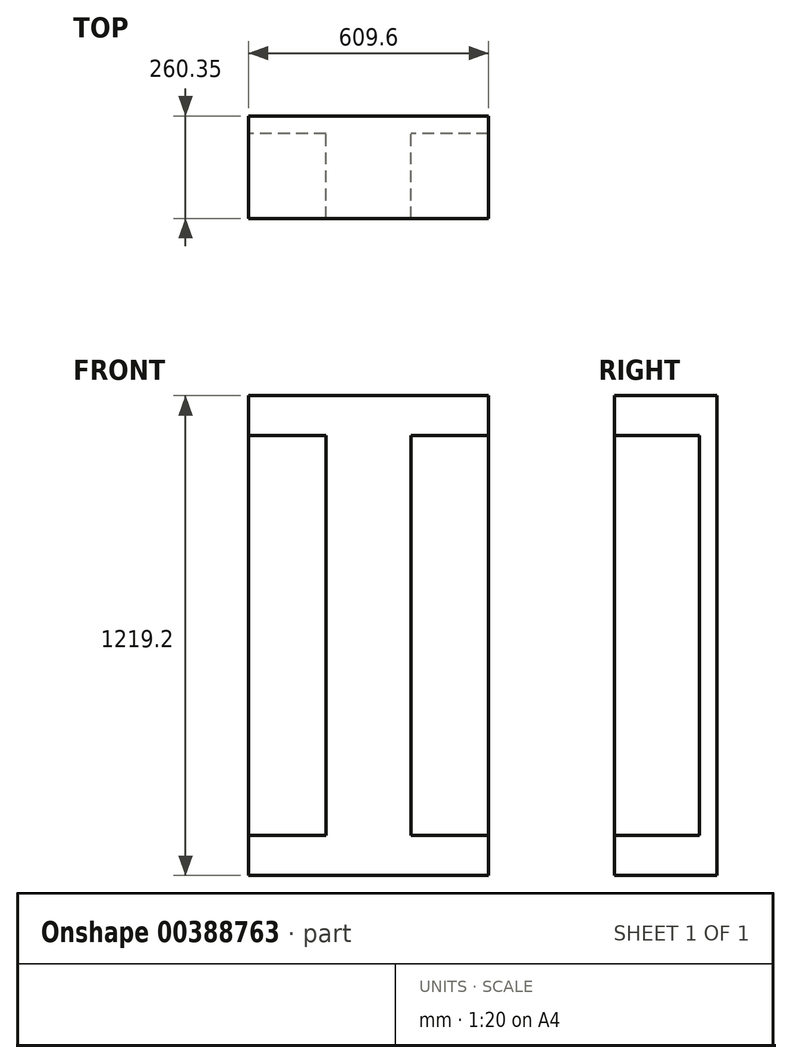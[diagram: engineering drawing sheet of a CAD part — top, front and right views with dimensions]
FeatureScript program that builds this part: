
annotation { "Feature Type Name" : "Feature", "Feature Type Description" : "" }
export const myFeature = defineFeature(function(context is Context, id is Id, definition is map)
    precondition{}
    {
        {
            var Q0;
            Q0=qCreatedBy(makeId("Front.planeOp"),FACE);
            var sketch = newSketch(context, id + "F0", { "sketchPlane" : qUnion([Q0])});
            skLineSegment(sketch, "E0.bottom", {"start": v(304.8, 609.6) * mm, "end": v(-304.8, 609.6) * mm});
            skLineSegment(sketch, "E0.top", {"start": v(304.8, -609.6) * mm, "end": v(-304.8, -609.6) * mm});
            skLineSegment(sketch, "E0.left", {"start": v(304.8, 609.6) * mm, "end": v(304.8, -609.6) * mm});
            skLineSegment(sketch, "E0.right", {"start": v(-304.8, 609.6) * mm, "end": v(-304.8, -609.6) * mm});
            skPoint(sketch, "E0.middle", {"position": v(0, 0) * mm});
            skSolve(sketch);
        }
        {
            var Q0;
            Q0=makeQuery(id+"F0.imprint","IMPRINT",FACE,{"disambiguationData":[TD([[makeQuery(id+"F0.imprint","IMPRINT",EDGE,{"derivedFrom":sQuery(id+"F0.wireOp",EDGE,"E0.bottom")}),1.0]])]});
            extrude(context, id + "F1", {"entities" : qUnion([Q0]), "depth" : 44.45 * mm});
        }
        {
            var Q0;
            Q0=makeQuery(id+"F1.opExtrude","CAP_FACE",FACE,{"disambiguationData":[OSD([sQuery(id+"F0.wireOp",EDGE,"E0.bottom"),sQuery(id+"F0.wireOp",EDGE,"E0.top"),sQuery(id+"F0.wireOp",EDGE,"E0.left"),sQuery(id+"F0.wireOp",EDGE,"E0.right")])],"isStart":false});
            var sketch = newSketch(context, id + "F2", { "sketchPlane" : qUnion([Q0])});
            skLineSegment(sketch, "E1.bottom", {"start": v(304.8, 609.6) * mm, "end": v(-304.8, 609.6) * mm});
            skLineSegment(sketch, "E1.top", {"start": v(304.8, 508) * mm, "end": v(-304.8, 508) * mm});
            skLineSegment(sketch, "E1.left", {"start": v(304.8, 609.6) * mm, "end": v(304.8, 508) * mm});
            skLineSegment(sketch, "E1.right", {"start": v(-304.8, 609.6) * mm, "end": v(-304.8, 508) * mm});
            skLineSegment(sketch, "E2", {"start": v(0, 0) * mm, "end": v(304.8, 0) * mm, "construction": true});
            skLineSegment(sketch, "E3.MirrorCS", {"start": v(304.8, -609.6) * mm, "end": v(-304.8, -609.6) * mm});
            skLineSegment(sketch, "E4.MirrorCS", {"start": v(304.8, -508) * mm, "end": v(-304.8, -508) * mm});
            skSolve(sketch);
        }
        {
            var Q0;
            Q0=makeQuery(id+"F2.imprint","IMPRINT",FACE,{"disambiguationData":[TD([[makeQuery(id+"F2.imprint","IMPRINT",EDGE,{"derivedFrom":sQuery(id+"F2.wireOp",EDGE,"E1.bottom")}),1.0]])]});
            var Q1;
            {var subQ0=sQuery(id+"F2.wireOp",EDGE,"E4.MirrorCS");Q1=makeQuery(id+"F2.imprint","IMPRINT",FACE,{"disambiguationData":[TD([[makeQuery(id+"F2.imprint","IMPRINT",EDGE,{"derivedFrom":subQ0}),1.0]])]});}
            extrude(context, id + "F3", {"entities" : qUnion([Q0, Q1]), "operationType" : NewBodyOperationType.ADD, "depth" : 215.9 * mm});
        }
        {
            var Q0;
            Q0=qCreatedBy(makeId("Front.planeOp"),FACE);
            var sketch = newSketch(context, id + "F4", { "sketchPlane" : qUnion([Q0])});
            skLineSegment(sketch, "E5.bottom", {"start": v(107.95, -508) * mm, "end": v(-107.95, -508) * mm});
            skLineSegment(sketch, "E5.top", {"start": v(107.95, 508) * mm, "end": v(-107.95, 508) * mm});
            skLineSegment(sketch, "E5.left", {"start": v(107.95, -508) * mm, "end": v(107.95, 508) * mm});
            skLineSegment(sketch, "E5.right", {"start": v(-107.95, -508) * mm, "end": v(-107.95, 508) * mm});
            skPoint(sketch, "E5.middle", {"position": v(0, 0) * mm});
            skSolve(sketch);
        }
        {
            var Q0;
            Q0 = qSketchRegion(id + "F4", true);
            extrude(context, id + "F5", {"entities" : qUnion([Q0]), "operationType" : NewBodyOperationType.ADD, "depth" : 260.35 * mm});
        }
    });
